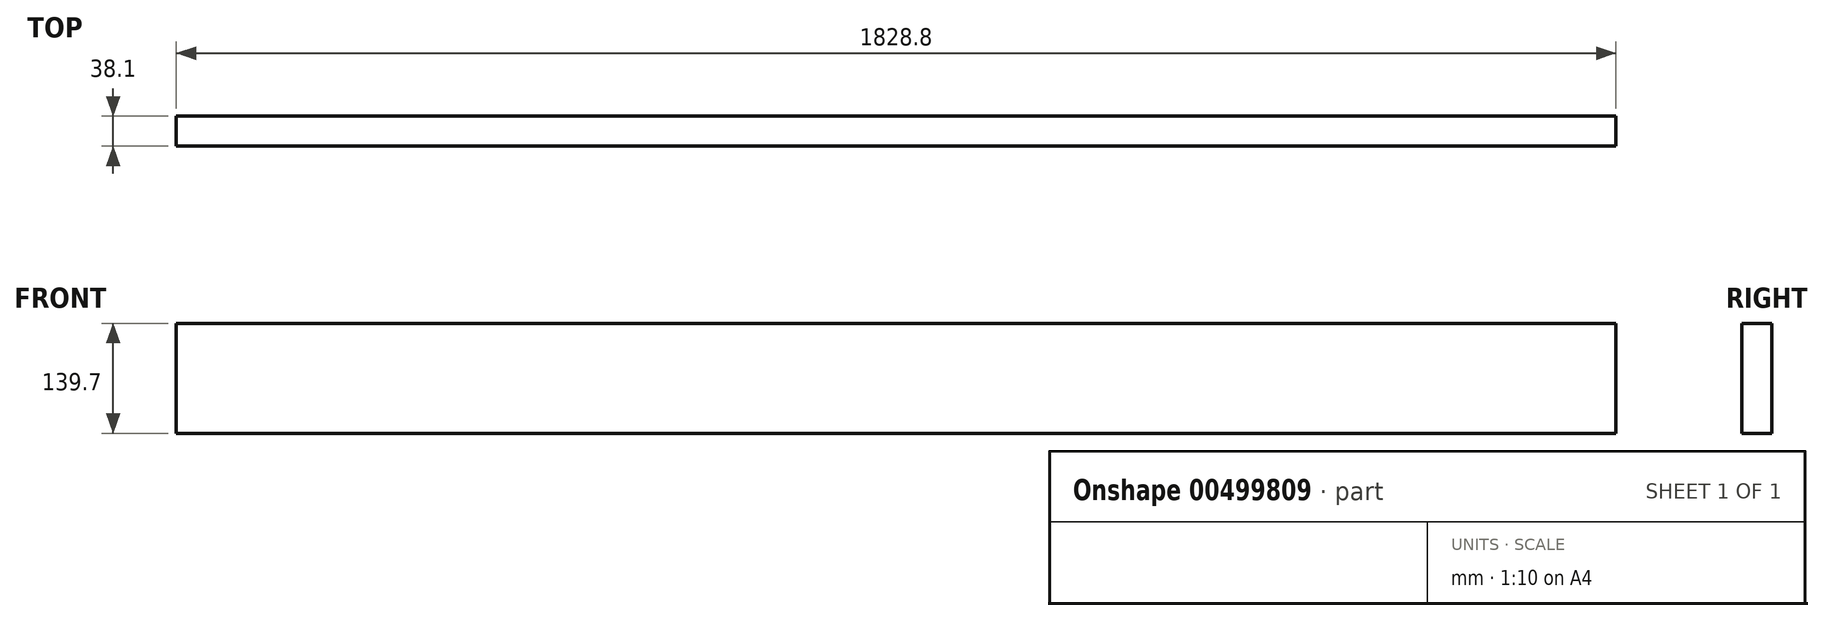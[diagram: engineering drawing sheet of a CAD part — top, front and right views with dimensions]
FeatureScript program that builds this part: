
annotation { "Feature Type Name" : "Feature", "Feature Type Description" : "" }
export const myFeature = defineFeature(function(context is Context, id is Id, definition is map)
    precondition{}
    {
        {
            var Q0;
            Q0=qCreatedBy(makeId("Front.planeOp"),FACE);
            var sketch = newSketch(context, id + "F0", { "sketchPlane" : qUnion([Q0])});
            skLineSegment(sketch, "E0.bottom", {"start": v(901.07, -69.85) * mm, "end": v(-927.73, -69.85) * mm});
            skLineSegment(sketch, "E0.top", {"start": v(901.07, 69.85) * mm, "end": v(-927.73, 69.85) * mm});
            skLineSegment(sketch, "E0.left", {"start": v(901.07, -69.85) * mm, "end": v(901.07, 69.85) * mm});
            skLineSegment(sketch, "E0.right", {"start": v(-927.73, -69.85) * mm, "end": v(-927.73, 69.85) * mm});
            skPoint(sketch, "E0.middle", {"position": v(-13.33, 0) * mm});
            skSolve(sketch);
        }
        {
            var Q0;
            Q0 = qSketchRegion(id + "F0", true);
            extrude(context, id + "F1", {"entities" : qUnion([Q0]), "depth" : 38.1 * mm});
        }
    });
